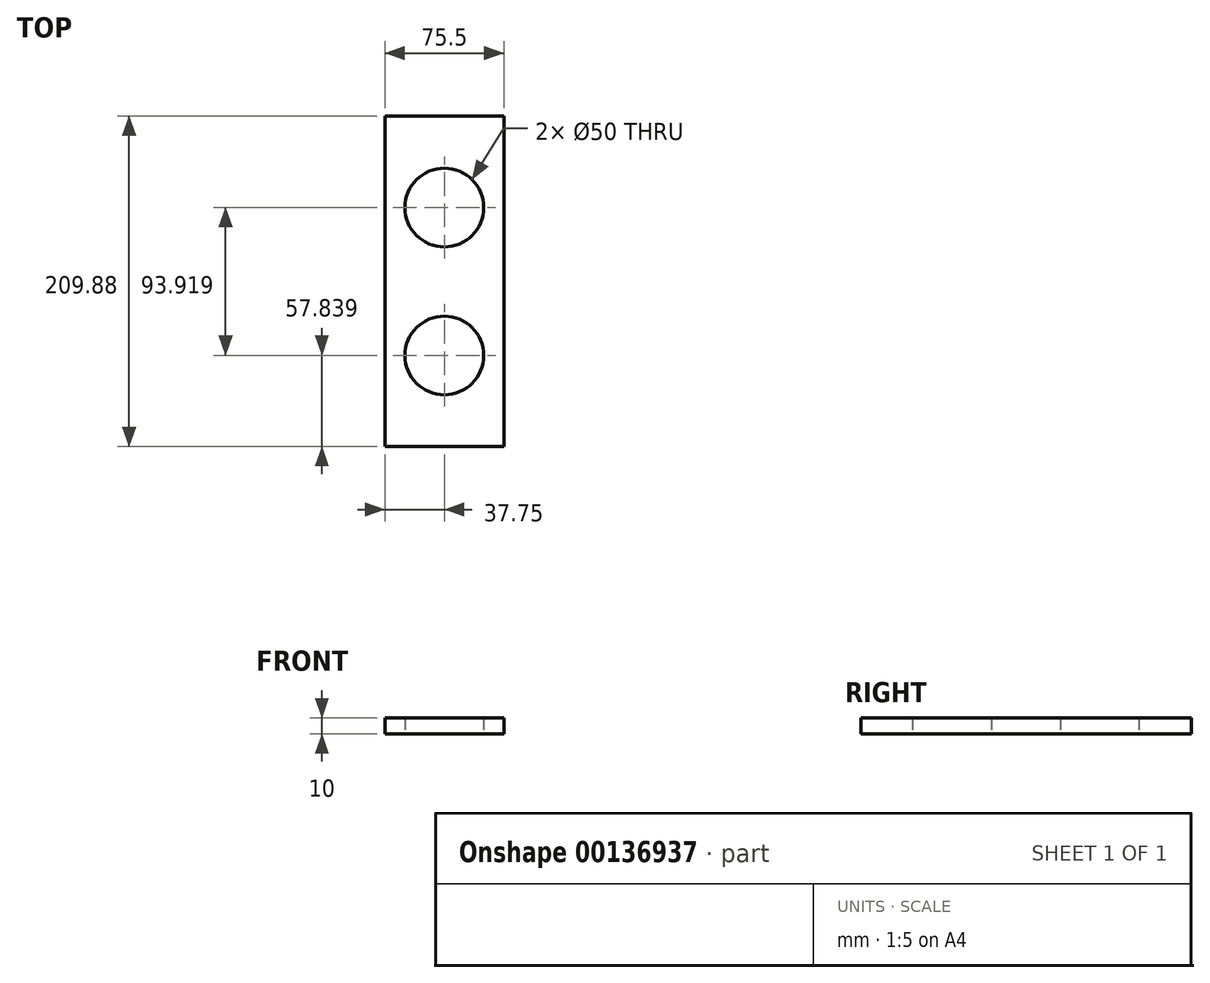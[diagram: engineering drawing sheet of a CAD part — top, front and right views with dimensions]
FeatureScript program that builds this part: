
annotation { "Feature Type Name" : "Feature", "Feature Type Description" : "" }
export const myFeature = defineFeature(function(context is Context, id is Id, definition is map)
    precondition{}
    {
        {
            var Q0;
            Q0=qCreatedBy(makeId("Top.planeOp"),FACE);
            var sketch = newSketch(context, id + "F0", { "sketchPlane" : qUnion([Q0])});
            skLineSegment(sketch, "E0.bottom", {"start": v(37.75, -104.94) * mm, "end": v(-37.75, -104.94) * mm});
            skLineSegment(sketch, "E0.top", {"start": v(37.75, 104.94) * mm, "end": v(-37.75, 104.94) * mm});
            skLineSegment(sketch, "E0.left", {"start": v(37.75, -104.94) * mm, "end": v(37.75, 104.94) * mm});
            skLineSegment(sketch, "E0.right", {"start": v(-37.75, -104.94) * mm, "end": v(-37.75, 104.94) * mm});
            skPoint(sketch, "E0.middle", {"position": v(0, 0) * mm});
            skCircle(sketch, "E1", {"center": v(0, 46.82) * mm, "radius": 25 * mm});
            skCircle(sketch, "E2", {"center": v(0, -47.1) * mm, "radius": 25 * mm});
            skLineSegment(sketch, "E3.bottom", {"start": v(27.5, 45.32) * mm, "end": v(-27.5, 45.32) * mm});
            skLineSegment(sketch, "E3.top", {"start": v(27.5, 48.32) * mm, "end": v(-27.5, 48.32) * mm});
            skLineSegment(sketch, "E3.left", {"start": v(27.5, 45.32) * mm, "end": v(27.5, 48.32) * mm});
            skLineSegment(sketch, "E3.right", {"start": v(-27.5, 45.32) * mm, "end": v(-27.5, 48.32) * mm});
            skLineSegment(sketch, "E4.bottom", {"start": v(27.5, -48.6) * mm, "end": v(-27.5, -48.6) * mm});
            skLineSegment(sketch, "E4.top", {"start": v(27.5, -45.6) * mm, "end": v(-27.5, -45.6) * mm});
            skLineSegment(sketch, "E4.left", {"start": v(27.5, -48.6) * mm, "end": v(27.5, -45.6) * mm});
            skLineSegment(sketch, "E4.right", {"start": v(-27.5, -48.6) * mm, "end": v(-27.5, -45.6) * mm});
            skSolve(sketch);
        }
        {
            var Q0;
            Q0=makeQuery(id+"F0.imprint","IMPRINT",FACE,{"disambiguationData":[TD([[makeQuery(id+"F0.imprint","IMPRINT",EDGE,{"derivedFrom":sQuery(id+"F0.wireOp",EDGE,"E0.bottom")}),-1.0]])]});
            var Q1;
            {var subQ5=sQuery(id+"F0.wireOp",EDGE,"E4.left");Q1=makeQuery(id+"F0.imprint","IMPRINT",FACE,{"disambiguationData":[TD([[makeQuery(id+"F0.imprint","IMPRINT",EDGE,{"derivedFrom":subQ5}),1.0]])]});}
            var Q2;
            {var subQ5=sQuery(id+"F0.wireOp",EDGE,"E4.right");Q2=makeQuery(id+"F0.imprint","IMPRINT",FACE,{"disambiguationData":[TD([[makeQuery(id+"F0.imprint","IMPRINT",EDGE,{"derivedFrom":subQ5}),-1.0]])]});}
            var Q3;
            {var subQ5=sQuery(id+"F0.wireOp",EDGE,"E3.right");Q3=makeQuery(id+"F0.imprint","IMPRINT",FACE,{"disambiguationData":[TD([[makeQuery(id+"F0.imprint","IMPRINT",EDGE,{"derivedFrom":subQ5}),-1.0]])]});}
            var Q4;
            {var subQ5=sQuery(id+"F0.wireOp",EDGE,"E3.left");Q4=makeQuery(id+"F0.imprint","IMPRINT",FACE,{"disambiguationData":[TD([[makeQuery(id+"F0.imprint","IMPRINT",EDGE,{"derivedFrom":subQ5}),1.0]])]});}
            extrude(context, id + "F1", {"entities" : qUnion([Q0, Q1, Q2, Q3, Q4]), "depth" : 10 * mm});
        }
    });
